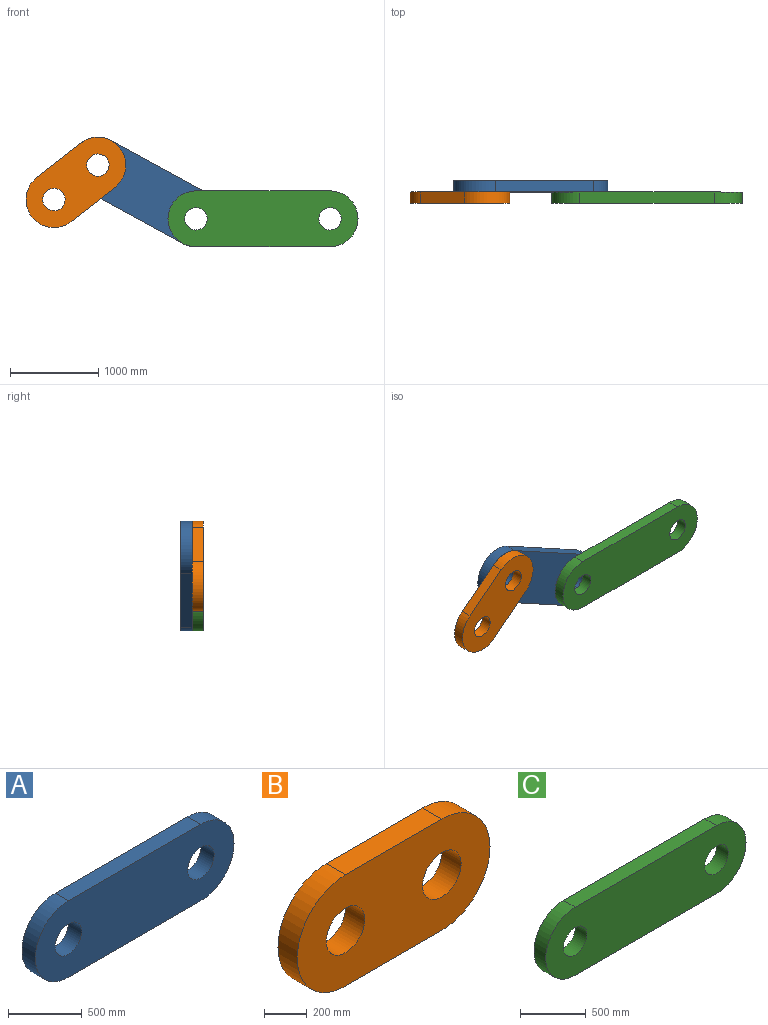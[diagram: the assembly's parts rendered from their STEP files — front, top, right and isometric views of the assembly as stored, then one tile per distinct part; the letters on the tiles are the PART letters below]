
ASSEMBLY  parts=3 mates=5
PART A: 8 faces, bbox 1905x127x635 mm
  f0: cylinder r=317.5mm len=635mm, axis (0,1,0), area 126676.9mm2, adj f1,f5,f6,f7
  f1: plane 1270x127mm, normal (0,0,-1), area 161290mm2, adj f0,f2,f6,f7
  f2: cylinder r=317.5mm len=635mm, axis (0,1,0), area 126676.9mm2, adj f1,f5,f6,f7
  f3: cylinder r=127mm len=254mm, axis (0,1,0), area 101341.5mm2, adj f6,f7
  f4: cylinder r=127mm len=254mm, axis (0,1,0), area 101341.5mm2, adj f6,f7
  f5: plane 1270x127mm, normal (0,0,1), area 161290mm2, adj f0,f2,f6,f7
  f6: plane 1905x635mm, normal (0,-1,0), area 1021800.7mm2, adj f0,f1,f2,f3,f4,f5
  f7: plane 1905x635mm, normal (0,1,0), area 1021800.7mm2, adj f0,f1,f2,f3,f4,f5
PART B: 8 faces, bbox 1270x127x635 mm
  f0: cylinder r=317.5mm len=635mm, axis (0,1,0), area 126676.9mm2, adj f1,f5,f6,f7
  f1: plane 635x127mm, normal (0,0,-1), area 80645mm2, adj f0,f2,f6,f7
  f2: cylinder r=317.5mm len=635mm, axis (0,1,0), area 126676.9mm2, adj f1,f5,f6,f7
  f3: cylinder r=127mm len=254mm, axis (0,1,0), area 101341.5mm2, adj f6,f7
  f4: cylinder r=127mm len=254mm, axis (0,1,0), area 101341.5mm2, adj f6,f7
  f5: plane 635x127mm, normal (0,0,1), area 80645mm2, adj f0,f2,f6,f7
  f6: plane 1270x635mm, normal (0,-1,0), area 618575.7mm2, adj f0,f1,f2,f3,f4,f5
  f7: plane 1270x635mm, normal (0,1,0), area 618575.7mm2, adj f0,f1,f2,f3,f4,f5
PART C: 8 faces, bbox 2159x127x635 mm
  f0: cylinder r=317.5mm len=635mm, axis (0,1,0), area 126676.9mm2, adj f1,f5,f6,f7
  f1: plane 1524x127mm, normal (0,0,-1), area 193548mm2, adj f0,f2,f6,f7
  f2: cylinder r=317.5mm len=635mm, axis (0,1,0), area 126676.9mm2, adj f1,f5,f6,f7
  f3: cylinder r=127mm len=254mm, axis (0,1,0), area 101341.5mm2, adj f6,f7
  f4: cylinder r=127mm len=254mm, axis (0,1,0), area 101341.5mm2, adj f6,f7
  f5: plane 1524x127mm, normal (0,0,1), area 193548mm2, adj f0,f2,f6,f7
  f6: plane 2159x635mm, normal (0,-1,0), area 1183090.7mm2, adj f0,f1,f2,f3,f4,f5
  f7: plane 2159x635mm, normal (0,1,0), area 1183090.7mm2, adj f0,f1,f2,f3,f4,f5
PLACE A rot(axis=(0,1,0),28.7deg) t=(-2080.95,1354.06,305.02)mm
PLACE B rot(axis=(0,1,0),141.9deg) t=(-2887.9,1227.06,414.33)mm
PLACE C t=(-762,1227.06,0)mm
MATE planar C.f2 <-> B.f6  axis (0,-1,0) through (0,1163.56,0)mm
MATE planar B.f7 <-> A.f6  axis (0,1,0) through (-2887.9,1290.56,414.33)mm
MATE planar A.f6 <-> C.f7  axis (0,-1,0) through (-2233.46,1290.56,26.55)mm
MATE cylindrical A.f2 <-> C.f0  axis (0,-1,0) through (-1524,1290.56,0)mm
MATE cylindrical A.f0 <-> B.f0  axis (0,-1,0) through (-2637.89,1290.56,610.04)mm
